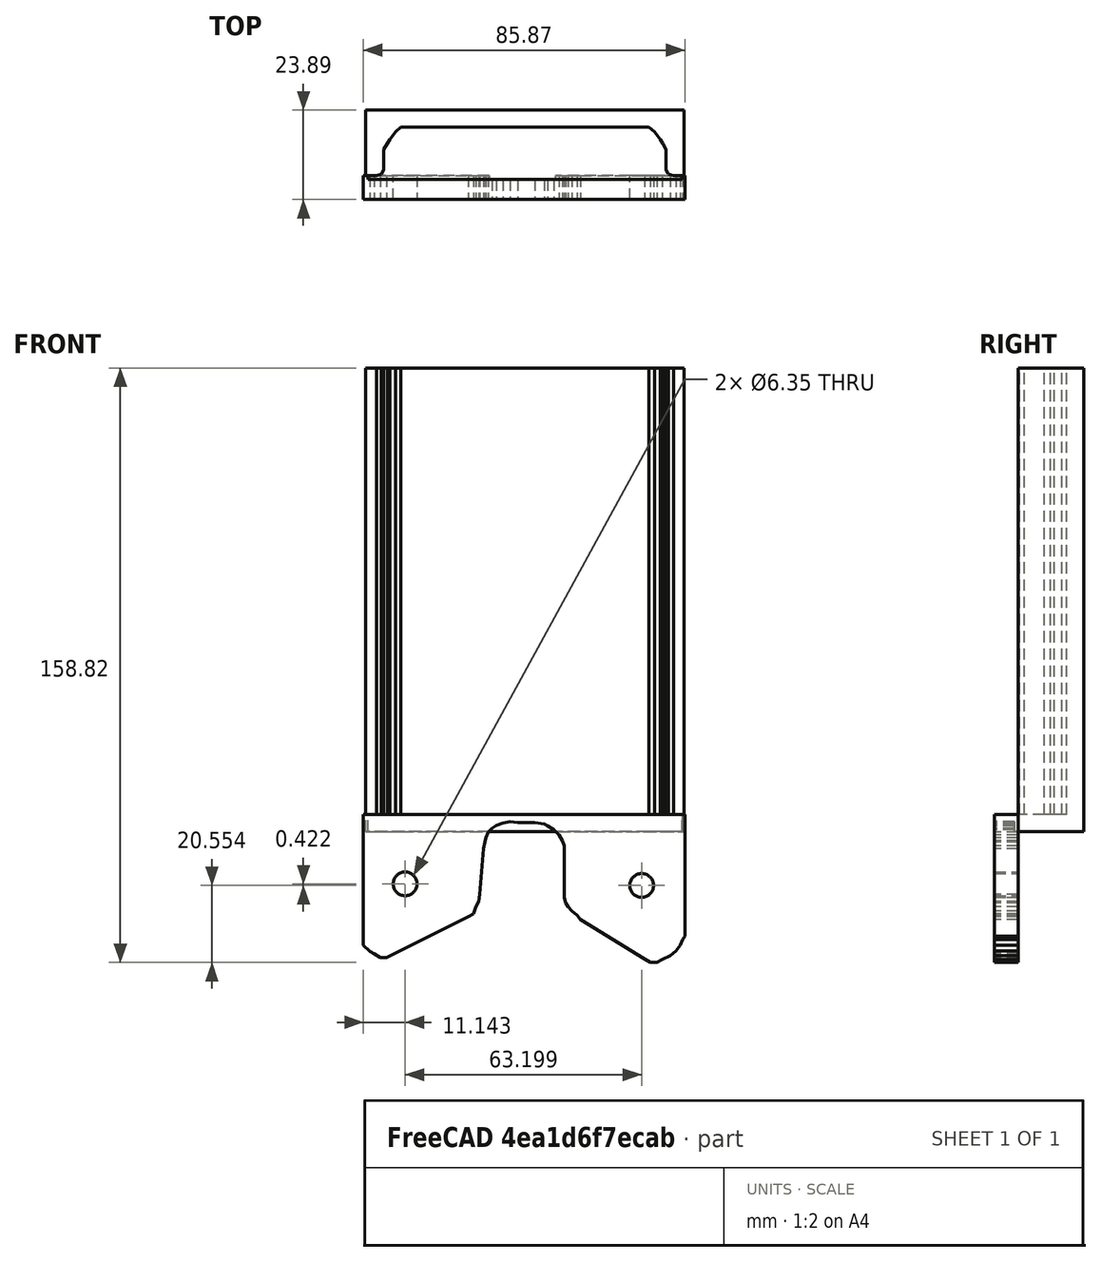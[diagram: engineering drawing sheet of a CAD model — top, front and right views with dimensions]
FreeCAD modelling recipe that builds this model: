
FCSTD DOCUMENT  (FreeCAD 0.20R29177 +426 (Git))
Label: logan-820-cross-slide-cover-model
License: All rights reserved
LicenseURL: http://en.wikipedia.org/wiki/All_rights_reserved
objects: Sketcher::SketchObject×8, Part::Extrusion×3, Mesh::Feature×2, Part::Box×1, Part::FeaturePython×1, Part::Feature×1
note: 14 computed .brp shape members not serialized (recipe doc carries the construction recipe); baked Part::Feature solids carry a one-line shape summary decoded from their .brp

FEATURE [Mesh::Feature] logan_820_cross_slide_cover_logan_cross_slide_bottom_located_new  label="logan-820-cross-slide-cover-logan-cross-slide-bottom-located-new"
FEATURE [Sketcher::SketchObject] Sketch  label="Sketch-through-holes"
  FullyConstrained = false
  MapMode = 3
  Placement = pos=(0,0,0) rot=(1,0,0;1.5708rad)
  Support = -> [logan_820_cross_slide_cover_logan_cross_slide_bottom_located_new]
  sketch-geometry (47):
    g0: Circle CenterX=-32.0171 CenterY=20.9758 CenterZ=0 NormalX=0 NormalY=0 NormalZ=1 AngleXU=0 Radius=3.175
    g1: Circle CenterX=31.1815 CenterY=20.5539 CenterZ=0 NormalX=0 NormalY=0 NormalZ=1 AngleXU=0 Radius=3.175
    g2: LineSegment StartX=-43.158 StartY=39.4781 StartZ=0 EndX=-43.158 EndY=4.59161 EndZ=0
    g3: LineSegment StartX=-43.158 StartY=4.59161 StartZ=0 EndX=-41.4153 EndY=2.95368 EndZ=0
    g4: LineSegment StartX=-41.4153 StartY=2.95368 StartZ=0 EndX=-40.2455 EndY=2.32143 EndZ=0
    g5: LineSegment StartX=-40.2455 StartY=2.32143 StartZ=0 EndX=-38.6261 EndY=1.23818 EndZ=0
    g6: LineSegment StartX=-38.6261 StartY=1.23818 StartZ=0 EndX=-37.0049 EndY=1.32572 EndZ=0
    g7: LineSegment StartX=-37.0049 StartY=1.32572 StartZ=0 EndX=-15.1932 EndY=12.1892 EndZ=0
    g8: LineSegment StartX=-15.1932 StartY=12.1892 StartZ=0 EndX=-13.751 EndY=12.9975 EndZ=0
    g9: LineSegment StartX=-13.751 StartY=12.9975 StartZ=0 EndX=-13.1176 EndY=14.8878 EndZ=0
    g10: LineSegment StartX=-13.1176 StartY=14.8878 StartZ=0 EndX=-12.3949 EndY=16.3276 EndZ=0
    g11: LineSegment StartX=-12.3949 StartY=16.3276 StartZ=0 EndX=-12.1219 EndY=18.1284 EndZ=0
    g12: LineSegment StartX=-12.1219 StartY=18.1284 StartZ=0 EndX=-11.1122 EndY=30.3751 EndZ=0
    g13: LineSegment StartX=-11.1122 StartY=30.3751 StartZ=0 EndX=-10.7491 EndY=32.1758 EndZ=0
    g14: LineSegment StartX=-10.7491 StartY=32.1758 StartZ=0 EndX=-10.3872 EndY=33.256 EndZ=0
    g15: LineSegment StartX=-10.3872 StartY=33.256 StartZ=0 EndX=-9.84445 EndY=34.7862 EndZ=0
    g16: LineSegment StartX=-9.84445 StartY=34.7862 StartZ=0 EndX=-8.76217 EndY=35.7752 EndZ=0
    g17: LineSegment StartX=-8.76217 StartY=35.7752 StartZ=0 EndX=-7.68018 EndY=36.584 EndZ=0
    g18: LineSegment StartX=-7.68018 StartY=36.584 StartZ=0 EndX=-5.87799 EndY=37.2116 EndZ=0
    g19: LineSegment StartX=-5.87799 StartY=37.2116 StartZ=0 EndX=-3.98615 EndY=37.5689 EndZ=0
    g20: LineSegment StartX=-3.98615 StartY=37.5689 StartZ=0 EndX=-1.91503 EndY=37.3856 EndZ=0
    g21: LineSegment StartX=-1.91503 StartY=37.3856 StartZ=0 EndX=0.516609 EndY=37.3856 EndZ=0
    g22: LineSegment StartX=0.516609 StartY=37.3856 StartZ=0 EndX=2.67807 EndY=37.3856 EndZ=0
    g23: LineSegment StartX=2.67807 StartY=37.3856 StartZ=0 EndX=5.10915 EndY=37.0144 EndZ=0
    g24: LineSegment StartX=5.10915 StartY=37.0144 StartZ=0 EndX=6.09898 EndY=36.4725 EndZ=0
    g25: LineSegment StartX=6.09898 StartY=36.4725 StartZ=0 EndX=7.71853 EndY=35.4793 EndZ=0
    g26: LineSegment StartX=7.71853 StartY=35.4793 StartZ=0 EndX=9.15727 EndY=34.0361 EndZ=0
    g27: LineSegment StartX=9.15727 StartY=34.0361 StartZ=0 EndX=9.96543 EndY=32.5038 EndZ=0
    g28: LineSegment StartX=9.96543 StartY=32.5038 StartZ=0 EndX=10.5037 EndY=31.1521 EndZ=0
    g29: LineSegment StartX=10.5037 StartY=31.1521 StartZ=0 EndX=10.5037 EndY=29.621 EndZ=0
    g30: LineSegment StartX=10.5037 StartY=29.621 StartZ=0 EndX=10.5037 EndY=17.283 EndZ=0
    g31: LineSegment StartX=10.5037 StartY=17.283 StartZ=0 EndX=10.8403 EndY=15.9312 EndZ=0
    g32: LineSegment StartX=10.8403 StartY=15.9312 StartZ=0 EndX=11.5591 EndY=14.8494 EndZ=0
    g33: LineSegment StartX=11.5591 StartY=14.8494 StartZ=0 EndX=12.548 EndY=13.7671 EndZ=0
    g34: LineSegment StartX=12.548 StartY=13.7671 StartZ=0 EndX=13.9872 EndY=12.5941 EndZ=0
    g35: LineSegment StartX=13.9872 StartY=12.5941 StartZ=0 EndX=14.7961 EndY=11.5121 EndZ=0
    g36: LineSegment StartX=14.7961 StartY=11.5121 StartZ=0 EndX=31.9812 EndY=0.85818 EndZ=0
    g37: LineSegment StartX=31.9812 StartY=0.85818 StartZ=0 EndX=33.5109 EndY=0 EndZ=0
    g38: LineSegment StartX=33.5109 StartY=0 StartZ=0 EndX=35.3127 EndY=0 EndZ=0
    g39: LineSegment StartX=35.3127 StartY=0 StartZ=0 EndX=36.6642 EndY=0.760835 EndZ=0
    g40: LineSegment StartX=36.6642 StartY=0.760835 StartZ=0 EndX=38.8273 EndY=1.8382 EndZ=0
    g41: LineSegment StartX=38.8273 StartY=1.8382 StartZ=0 EndX=40.3602 EndY=3.00661 EndZ=0
    g42: LineSegment StartX=40.3602 StartY=3.00661 StartZ=0 EndX=41.4433 EndY=4.53596 EndZ=0
    g43: LineSegment StartX=41.4433 StartY=4.53596 StartZ=0 EndX=42.0762 EndY=6.15608 EndZ=0
    g44: LineSegment StartX=42.0762 StartY=6.15608 StartZ=0 EndX=42.7079 EndY=6.96564 EndZ=0
    g45: LineSegment StartX=42.7079 StartY=6.96564 StartZ=0 EndX=42.7079 EndY=39.4781 EndZ=0
    g46: LineSegment StartX=42.7079 StartY=39.4781 StartZ=0 EndX=-43.158 EndY=39.4781 EndZ=0
  constraints (57):
    c: Distance(g1,g0) = 63.2
    c: Diameter(g0) = 6.35
    c: Diameter(g1) = 6.35
    c: Vertical(g2)
    c: Coincident(g2,g3)
    c: Coincident(g3,g4)
    c: Coincident(g4,g5)
    c: Coincident(g5,g6)
    c: Coincident(g6,g7)
    c: Coincident(g7,g8)
    c: Coincident(g8,g9)
    c: Coincident(g9,g10)
    c: Coincident(g10,g11)
    c: Coincident(g11,g12)
    c: Coincident(g12,g13)
    c: Coincident(g13,g14)
    c: Coincident(g14,g15)
    c: Coincident(g15,g16)
    c: Coincident(g16,g17)
    c: Coincident(g17,g18)
    c: Coincident(g18,g19)
    c: Coincident(g19,g20)
    c: Coincident(g20,g21)
    c: Horizontal(g21)
    c: Coincident(g21,g22)
    c: Horizontal(g22)
    c: Coincident(g22,g23)
    c: Coincident(g23,g24)
    c: Coincident(g24,g25)
    c: Coincident(g25,g26)
    c: Coincident(g26,g27)
    c: Coincident(g27,g28)
    c: Coincident(g28,g29)
    c: Vertical(g29)
    c: Coincident(g29,g30)
    c: Vertical(g30)
    c: Coincident(g30,g31)
    c: Coincident(g31,g32)
    c: Coincident(g32,g33)
    c: Coincident(g33,g34)
    c: Coincident(g34,g35)
    c: Coincident(g35,g36)
    c: Coincident(g36,g37)
    c: PointOnObject(g37,g-1)
    c: Coincident(g37,g38)
    c: PointOnObject(g38,g-1)
    c: Coincident(g38,g39)
    c: Coincident(g39,g40)
    c: Coincident(g40,g41)
    c: Coincident(g41,g42)
    c: Coincident(g42,g43)
    c: Coincident(g43,g44)
    c: Coincident(g44,g45)
    c: Vertical(g45)
    c: Coincident(g45,g46)
    c: Coincident(g46,g2)
    c: Horizontal(g46)
FEATURE [Sketcher::SketchObject] Sketch001  label="sketch-side"
  FullyConstrained = false
  MapMode = 4
  Placement = pos=(0,0,0) rot=(0.707107,0,0.707107;3.14159rad)
  Support = -> [Sketch]
  sketch-geometry (23):
    g0: LineSegment StartX=41.088 StartY=-4.31506 StartZ=0 EndX=39.2016 EndY=-13.0361 EndZ=0
    g1: LineSegment StartX=39.2016 StartY=-13.0361 StartZ=0 EndX=38.7187 EndY=-13.8209 EndZ=0
    g2: LineSegment StartX=38.7187 StartY=-13.8209 StartZ=0 EndX=37.9943 EndY=-14.7264 EndZ=0
    g3: LineSegment StartX=37.9943 StartY=-14.7264 StartZ=0 EndX=37.0283 EndY=-14.9075 EndZ=0
    g4: LineSegment StartX=37.0283 StartY=-14.9075 StartZ=0 EndX=36.0624 EndY=-15.149 EndZ=0
    g5: LineSegment StartX=36.0624 StartY=-15.149 StartZ=0 EndX=4.10285 EndY=-13.8406 EndZ=0
    g6: LineSegment StartX=4.10285 StartY=-13.8406 StartZ=0 EndX=3.29351 EndY=-13.962 EndZ=0
    g7: LineSegment StartX=3.29351 StartY=-13.962 StartZ=0 EndX=2.40323 EndY=-14.1238 EndZ=0
    g8: LineSegment StartX=2.40323 StartY=-14.1238 StartZ=0 EndX=1.59389 EndY=-14.6095 EndZ=0
    g9: LineSegment StartX=1.59389 StartY=-14.6095 StartZ=0 EndX=1.14876 EndY=-14.9332 EndZ=0
    g10: LineSegment StartX=1.14876 StartY=-14.9332 StartZ=0 EndX=0.905955 EndY=-15.4188 EndZ=0
    g11: LineSegment StartX=0.905955 StartY=-15.4188 StartZ=0 EndX=0.744088 EndY=-16.2281 EndZ=0
    g12: LineSegment StartX=0.744088 StartY=-16.2281 StartZ=0 EndX=0.460819 EndY=-19.2632 EndZ=0
    g13: LineSegment StartX=0.460819 StartY=-19.2632 StartZ=0 EndX=42.3738 EndY=-19.2632 EndZ=0
    g14: LineSegment StartX=42.3738 StartY=-19.2632 StartZ=0 EndX=42.9637 EndY=-18.7401 EndZ=0
    g15: LineSegment StartX=42.9637 StartY=-18.7401 StartZ=0 EndX=43.9223 EndY=-17.8553 EndZ=0
    g16: LineSegment StartX=43.9223 StartY=-17.8553 StartZ=0 EndX=44.291 EndY=-16.6755 EndZ=0
    g17: LineSegment StartX=44.291 StartY=-16.6755 StartZ=0 EndX=163.958 EndY=-16.6755 EndZ=0
    g18: LineSegment StartX=163.958 StartY=-16.6755 StartZ=0 EndX=162.557 EndY=-5.78977 EndZ=0
    g19: LineSegment StartX=162.557 StartY=-5.78977 StartZ=0 EndX=161.967 EndY=-5.12615 EndZ=0
    g20: LineSegment StartX=161.967 StartY=-5.12615 StartZ=0 EndX=161.156 EndY=-4.83121 EndZ=0
    g21: LineSegment StartX=161.156 StartY=-4.83121 StartZ=0 EndX=159.755 EndY=-4.31506 EndZ=0
    g22: LineSegment StartX=159.755 StartY=-4.31506 StartZ=0 EndX=41.088 EndY=-4.31506 EndZ=0
  constraints (26):
    c: Coincident(g0,g1)
    c: Coincident(g1,g2)
    c: Coincident(g2,g3)
    c: Coincident(g3,g4)
    c: Coincident(g4,g5)
    c: Coincident(g5,g6)
    c: Coincident(g6,g7)
    c: Coincident(g7,g8)
    c: Coincident(g8,g9)
    c: Coincident(g9,g10)
    c: Coincident(g10,g11)
    c: Coincident(g11,g12)
    c: Coincident(g12,g13)
    c: Horizontal(g13)
    c: Coincident(g13,g14)
    c: Coincident(g14,g15)
    c: Coincident(g15,g16)
    c: Coincident(g16,g17)
    c: Horizontal(g17)
    c: Coincident(g17,g18)
    c: Coincident(g18,g19)
    c: Coincident(g19,g20)
    c: Coincident(g20,g21)
    c: Coincident(g21,g22)
    c: Coincident(g22,g0)
    c: Horizontal(g22)
FEATURE [Sketcher::SketchObject] Sketch002  label="sketch-side-of-mount"
  FullyConstrained = false
  MapMode = 4
  Placement = pos=(0,0,0) rot=(0.707107,0,0.707107;3.14159rad)
  Support = -> [Sketch]
  sketch-geometry (23):
    g0: LineSegment StartX=45.8302 StartY=-2.4673 StartZ=0 EndX=43.8508 EndY=-1.76256 EndZ=0
    g1: LineSegment StartX=43.8508 StartY=-1.76256 StartZ=0 EndX=42.5311 EndY=-1.76256 EndZ=0
    g2: LineSegment StartX=42.5311 StartY=-1.76256 StartZ=0 EndX=41.3419 EndY=-2.70137 EndZ=0
    g3: LineSegment StartX=41.3419 StartY=-2.70137 StartZ=0 EndX=40.7205 EndY=-4.36669 EndZ=0
    g4: LineSegment StartX=40.7205 StartY=-4.36669 StartZ=0 EndX=39.1914 EndY=-14.3075 EndZ=0
    g5: LineSegment StartX=39.1914 StartY=-14.3075 StartZ=0 EndX=38.5546 EndY=-15.3128 EndZ=0
    g6: LineSegment StartX=38.5546 StartY=-15.3128 StartZ=0 EndX=37.46 EndY=-15.5584 EndZ=0
    g7: LineSegment StartX=37.46 StartY=-15.5584 StartZ=0 EndX=36.4703 EndY=-15.5584 EndZ=0
    g8: LineSegment StartX=36.4703 StartY=-15.5584 StartZ=0 EndX=3.92285 EndY=-15.5584 EndZ=0
    g9: LineSegment StartX=3.92285 StartY=-15.5584 StartZ=0 EndX=2.8393 EndY=-14.8509 EndZ=0
    g10: LineSegment StartX=2.8393 StartY=-14.8509 StartZ=0 EndX=1.93962 EndY=-15.1134 EndZ=0
    g11: LineSegment StartX=1.93962 StartY=-15.1134 StartZ=0 EndX=1.34593 EndY=-15.55 EndZ=0
    g12: LineSegment StartX=1.34593 StartY=-15.55 StartZ=0 EndX=0.879963 EndY=-16.2857 EndZ=0
    g13: LineSegment StartX=0.879963 StartY=-16.2857 StartZ=0 EndX=0.654005 EndY=-16.9553 EndZ=0
    g14: LineSegment StartX=0.654005 StartY=-16.9553 StartZ=0 EndX=0.654005 EndY=-18.5249 EndZ=0
    g15: LineSegment StartX=0.654005 StartY=-18.5249 StartZ=0 EndX=0.346687 EndY=-19.3181 EndZ=0
    g16: LineSegment StartX=0.346687 StartY=-19.3181 StartZ=0 EndX=0.178274 EndY=-19.8656 EndZ=0
    g17: LineSegment StartX=0.178274 StartY=-19.8656 StartZ=0 EndX=38.3328 EndY=-19.8656 EndZ=0
    g18: LineSegment StartX=38.3328 StartY=-19.8656 StartZ=0 EndX=42.7484 EndY=-19.8656 EndZ=0
    g19: LineSegment StartX=42.7484 StartY=-19.8656 StartZ=0 EndX=45.3112 EndY=-15.7356 EndZ=0
    g20: LineSegment StartX=45.3112 StartY=-15.7356 StartZ=0 EndX=70.0028 EndY=-15.7356 EndZ=0
    g21: LineSegment StartX=70.0028 StartY=-15.7356 StartZ=0 EndX=70.0028 EndY=-2.4673 EndZ=0
    g22: LineSegment StartX=70.0028 StartY=-2.4673 StartZ=0 EndX=45.8302 EndY=-2.4673 EndZ=0
  constraints (32):
    c: Coincident(g0,g1)
    c: Horizontal(g1)
    c: Coincident(g1,g2)
    c: Coincident(g2,g3)
    c: Coincident(g3,g4)
    c: Coincident(g4,g5)
    c: Coincident(g5,g6)
    c: Coincident(g6,g7)
    c: Horizontal(g7)
    c: Coincident(g7,g8)
    c: Horizontal(g8)
    c: Coincident(g8,g9)
    c: Coincident(g9,g10)
    c: Coincident(g10,g11)
    c: Coincident(g11,g12)
    c: Coincident(g12,g13)
    c: Coincident(g13,g14)
    c: Vertical(g14)
    c: Coincident(g14,g15)
    c: Coincident(g15,g16)
    c: Coincident(g16,g17)
    c: Horizontal(g17)
    c: Coincident(g17,g18)
    c: Horizontal(g18)
    c: Coincident(g18,g19)
    c: Coincident(g19,g20)
    c: Horizontal(g20)
    c: Coincident(g20,g21)
    c: Vertical(g21)
    c: Coincident(g21,g22)
    c: Coincident(g22,g0)
    c: Horizontal(g22)
FEATURE [Sketcher::SketchObject] Sketch003  label="sketch-end"
  FullyConstrained = false
  sketch-geometry (26):
    g0: LineSegment StartX=-43.5422 StartY=19.1592 StartZ=0 EndX=-43.5422 EndY=0.579213 EndZ=0
    g1: LineSegment StartX=-43.5422 StartY=0.579213 StartZ=0 EndX=-40.4943 EndY=0.579213 EndZ=0
    g2: LineSegment StartX=-40.4943 StartY=0.579213 StartZ=0 EndX=-39.3512 EndY=0.877175 EndZ=0
    g3: LineSegment StartX=-39.3512 StartY=0.877175 StartZ=0 EndX=-38.5964 EndY=3.02767 EndZ=0
    g4: LineSegment StartX=-38.5964 StartY=3.02767 StartZ=0 EndX=-38.5421 EndY=6.3087 EndZ=0
    g5: LineSegment StartX=-38.5421 StartY=6.3087 StartZ=0 EndX=-38.3105 EndY=8.54246 EndZ=0
    g6: LineSegment StartX=-38.3105 StartY=8.54246 StartZ=0 EndX=-37.4257 EndY=10.5333 EndZ=0
    g7: LineSegment StartX=-37.4257 StartY=10.5333 StartZ=0 EndX=-35.656 EndY=12.2292 EndZ=0
    g8: LineSegment StartX=-35.656 StartY=12.2292 StartZ=0 EndX=-34.1813 EndY=13.409 EndZ=0
    g9: LineSegment StartX=-34.1813 StartY=13.409 StartZ=0 EndX=-32.7803 EndY=13.704 EndZ=0
    g10: LineSegment StartX=-32.7803 StartY=13.704 StartZ=0 EndX=30.8535 EndY=13.704 EndZ=0
    g11: LineSegment StartX=30.8535 StartY=13.704 StartZ=0 EndX=33.213 EndY=13.0403 EndZ=0
    g12: LineSegment StartX=33.213 StartY=13.0403 StartZ=0 EndX=34.3191 EndY=12.2292 EndZ=0
    g13: LineSegment StartX=34.3191 StartY=12.2292 StartZ=0 EndX=35.8675 EndY=10.6808 EndZ=0
    g14: LineSegment StartX=35.8675 StartY=10.6808 StartZ=0 EndX=37.0473 EndY=8.8374 EndZ=0
    g15: LineSegment StartX=37.0473 StartY=8.8374 StartZ=0 EndX=37.1948 EndY=7.65763 EndZ=0
    g16: LineSegment StartX=37.1948 StartY=7.65763 StartZ=0 EndX=37.4897 EndY=6.5516 EndZ=0
    g17: LineSegment StartX=37.4897 StartY=6.5516 StartZ=0 EndX=38.0796 EndY=2.86482 EndZ=0
    g18: LineSegment StartX=38.0796 StartY=2.86482 StartZ=0 EndX=38.5957 EndY=1.68505 EndZ=0
    g19: LineSegment StartX=38.5957 StartY=1.68505 StartZ=0 EndX=39.2594 EndY=1.09516 EndZ=0
    g20: LineSegment StartX=39.2594 StartY=1.09516 StartZ=0 EndX=39.923 EndY=0.583043 EndZ=0
    g21: LineSegment StartX=39.923 StartY=0.583043 StartZ=0 EndX=42.2078 EndY=0.583043 EndZ=0
    g22: LineSegment StartX=42.2078 StartY=0.583043 StartZ=0 EndX=42.2078 EndY=19.163 EndZ=0
    g23: LineSegment StartX=42.2078 StartY=19.163 StartZ=0 EndX=-43.5422 EndY=19.163 EndZ=0
    g24: GeomPoint X=-39.0502 Y=1.73483 Z=0
    g25: GeomPoint X=-40.412 Y=0.600657 Z=0
  constraints (34):
    c: Vertical(g0)
    c: Coincident(g0,g1)
    c: Coincident(g1,g2)
    c: Coincident(g2,g3)
    c: Coincident(g3,g4)
    c: Coincident(g4,g5)
    c: Coincident(g5,g6)
    c: Coincident(g6,g7)
    c: Coincident(g7,g8)
    c: Coincident(g8,g9)
    c: Coincident(g9,g10)
    c: Horizontal(g10)
    c: Coincident(g10,g11)
    c: Coincident(g11,g12)
    c: Coincident(g12,g13)
    c: Coincident(g13,g14)
    c: Coincident(g14,g15)
    c: Coincident(g15,g16)
    c: Coincident(g16,g17)
    c: Coincident(g17,g18)
    c: Coincident(g18,g19)
    c: Coincident(g19,g20)
    c: Coincident(g20,g21)
    c: Coincident(g21,g22)
    c: Vertical(g22)
    c: Coincident(g22,g23)
    c: Horizontal(g23)
    c: Horizontal(g21)
    c: Distance(g23) = 85.75
    c: Distance(g22) = 18.58
    c: Equal(g0,g22)
    c: PointOnObject(g24,g3)
    c: PointOnObject(g25,g2)
    c: Horizontal(g1)
FEATURE [Part::Extrusion] Extrude  label="Extrude-main-cover-first-attempt"
  Base = -> Sketch003
  Dir = (0,0,1)
  DirMode = 2
  FaceMakerClass = Part::FaceMakerBullseye
  LengthFwd = 120.65
  LengthRev = 0
  Placement = pos=(0,0,38.1) rot=(0,0,1;0rad)
  Solid = false
  Symmetric = false
FEATURE [Part::Extrusion] Extrude001  label="extrude-mount"
  Base = -> Sketch
  Dir = (0,-1,2e-16)
  DirMode = 2
  FaceMakerClass = Part::FaceMakerBullseye
  LengthFwd = 6.35
  LengthRev = 0
  Solid = true
  Symmetric = false
FEATURE [Sketcher::SketchObject] Sketch004  label="sketch-end-half"
  FullyConstrained = false
  sketch-geometry (20):
    g0: LineSegment StartX=-0.0341461 StartY=13.7403 StartZ=0 EndX=30.8542 EndY=13.7403 EndZ=0
    g1: LineSegment StartX=30.8542 StartY=13.7403 StartZ=0 EndX=33.213 EndY=13.0403 EndZ=0
    g2: LineSegment StartX=33.213 StartY=13.0403 StartZ=0 EndX=34.3191 EndY=12.2292 EndZ=0
    g3: LineSegment StartX=34.3191 StartY=12.2292 StartZ=0 EndX=35.8675 EndY=10.6808 EndZ=0
    g4: LineSegment StartX=35.8675 StartY=10.6808 StartZ=0 EndX=37.0473 EndY=8.8374 EndZ=0
    g5: LineSegment StartX=37.0473 StartY=8.8374 StartZ=0 EndX=37.251 EndY=7.64431 EndZ=0
    g6: LineSegment StartX=37.251 StartY=7.64431 StartZ=0 EndX=37.4897 EndY=6.5516 EndZ=0
    g7: LineSegment StartX=37.4897 StartY=6.5516 StartZ=0 EndX=38.0796 EndY=2.86482 EndZ=0
    g8: LineSegment StartX=38.0796 StartY=2.86482 StartZ=0 EndX=38.5957 EndY=1.68505 EndZ=0
    g9: LineSegment StartX=38.5957 StartY=1.68505 StartZ=0 EndX=39.2594 EndY=1.09516 EndZ=0
    g10: LineSegment StartX=39.2594 StartY=1.09516 StartZ=0 EndX=39.93 EndY=0.6 EndZ=0
    g11: LineSegment StartX=39.93 StartY=0.6 StartZ=0 EndX=42.21 EndY=0.6 EndZ=0
    g12: LineSegment StartX=42.21 StartY=0.6 StartZ=0 EndX=42.21 EndY=19.18 EndZ=0
    g13: LineSegment StartX=42.21 StartY=19.18 StartZ=0 EndX=-43.54 EndY=19.18 EndZ=0
    g14: GeomPoint X=-0.0903729 Y=19.18 Z=0
    g15: GeomPoint X=-0.025795 Y=13.7403 Z=0
    g16: GeomPoint X=42.21 Y=0 Z=0
    g17: GeomPoint X=39.93 Y=0 Z=0
    g18: GeomPoint X=0 Y=0.6 Z=0
    g19: GeomPoint X=42.21 Y=13.3891 Z=0
  constraints (32):
    c: Horizontal(g0)
    c: Coincident(g0,g1)
    c: Coincident(g1,g2)
    c: Coincident(g2,g3)
    c: Coincident(g3,g4)
    c: Coincident(g4,g5)
    c: Coincident(g5,g6)
    c: Coincident(g6,g7)
    c: Coincident(g7,g8)
    c: Coincident(g8,g9)
    c: Coincident(g9,g10)
    c: Coincident(g10,g11)
    c: Coincident(g11,g12)
    c: Vertical(g12)
    c: Coincident(g12,g13)
    c: Horizontal(g13)
    c: Horizontal(g11)
    c: Distance(g13) = 85.75
    c: Distance(g12) = 18.58
    c: PointOnObject(g14,g13)
    c: PointOnObject(g15,g0)
    c: PointOnObject(g16,g-1)
    c: PointOnObject(g17,g-1)
    c: Distance(g16,g11) = 0.6
    c: Distance(g10,g17) = 0.6
    c: PointOnObject(g18,g-2)
    c: Distance(g-1,g18) = 0.6
    c: Distance(g18,g11) = 42.21
    c: Distance(g10,g11) = 2.28
    c: Distance(g0,g15) = 30.88
    c: PointOnObject(g19,g12)
    c: Distance(g14,g0) = 5.44
FEATURE [Sketcher::SketchObject] Sketch005
  FullyConstrained = false
  sketch-geometry (13):
    g0: LineSegment StartX=0 StartY=18.5413 StartZ=0 EndX=42.57 EndY=18.5413 EndZ=0
    g1: LineSegment StartX=42.57 StartY=18.5413 StartZ=0 EndX=42.57 EndY=1.01296 EndZ=0
    g2: LineSegment StartX=42.57 StartY=1.01296 StartZ=0 EndX=39.6826 EndY=1.01296 EndZ=0
    g3: LineSegment StartX=39.6826 StartY=1.01296 StartZ=0 EndX=38.3774 EndY=1.3859 EndZ=0
    g4: LineSegment StartX=38.3774 StartY=1.3859 StartZ=0 EndX=37.7247 EndY=2.59796 EndZ=0
    g5: LineSegment StartX=37.7247 StartY=2.59796 StartZ=0 EndX=37.7247 EndY=8.00564 EndZ=0
    g6: LineSegment StartX=37.7247 StartY=8.00564 StartZ=0 EndX=36.7923 EndY=9.68388 EndZ=0
    g7: LineSegment StartX=36.7923 StartY=9.68388 StartZ=0 EndX=36.1211 EndY=10.6977 EndZ=0
    g8: LineSegment StartX=36.1211 StartY=10.6977 StartZ=0 EndX=34.642 EndY=12.6601 EndZ=0
    g9: LineSegment StartX=34.642 StartY=12.6601 StartZ=0 EndX=33.1688 EndY=13.9727 EndZ=0
    g10: LineSegment StartX=33.1688 StartY=13.9727 StartZ=0 EndX=0 EndY=13.9727 EndZ=0
    g11: LineSegment StartX=0 StartY=13.9727 StartZ=0 EndX=0 EndY=18.5413 EndZ=0
    g12: GeomPoint X=42.57 Y=14.0374 Z=0
  constraints (21):
    c: PointOnObject(g0,g-2)
    c: Horizontal(g0)
    c: Coincident(g0,g1)
    c: Vertical(g1)
    c: Coincident(g1,g2)
    c: Horizontal(g2)
    c: Coincident(g2,g3)
    c: Coincident(g3,g4)
    c: Coincident(g4,g5)
    c: Coincident(g5,g6)
    c: Coincident(g6,g7)
    c: Coincident(g7,g8)
    c: Coincident(g8,g9)
    c: Coincident(g9,g10)
    c: PointOnObject(g10,g-2)
    c: Coincident(g10,g11)
    c: PointOnObject(g11,g-2)
    c: Horizontal(g10)
    c: Vertical(g5)
    c: Distance(g0) = 42.57
    c: PointOnObject(g12,g1)
FEATURE [Sketcher::SketchObject] MirroredSketch
  FullyConstrained = false
  Placement = pos=(-1,0,0) rot=(0,0,1;0rad)
  sketch-geometry (13):
    g0: LineSegment StartX=0 StartY=18.5413 StartZ=0 EndX=-42.57 EndY=18.5413 EndZ=0
    g1: LineSegment StartX=-42.57 StartY=18.5413 StartZ=0 EndX=-42.57 EndY=1.01296 EndZ=0
    g2: LineSegment StartX=-42.57 StartY=1.01296 StartZ=0 EndX=-39.6826 EndY=1.01296 EndZ=0
    g3: LineSegment StartX=-39.6826 StartY=1.01296 StartZ=0 EndX=-38.3774 EndY=1.3859 EndZ=0
    g4: LineSegment StartX=-38.3774 StartY=1.3859 StartZ=0 EndX=-37.7247 EndY=2.59796 EndZ=0
    g5: LineSegment StartX=-37.7247 StartY=2.59796 StartZ=0 EndX=-37.7247 EndY=8.00564 EndZ=0
    g6: LineSegment StartX=-37.7247 StartY=8.00564 StartZ=0 EndX=-36.7923 EndY=9.68388 EndZ=0
    g7: LineSegment StartX=-36.7923 StartY=9.68388 StartZ=0 EndX=-36.1211 EndY=10.6977 EndZ=0
    g8: LineSegment StartX=-36.1211 StartY=10.6977 StartZ=0 EndX=-34.642 EndY=12.6601 EndZ=0
    g9: LineSegment StartX=-34.642 StartY=12.6601 StartZ=0 EndX=-33.1688 EndY=13.9727 EndZ=0
    g10: LineSegment StartX=-33.1688 StartY=13.9727 StartZ=0 EndX=0 EndY=13.9727 EndZ=0
    g11: LineSegment StartX=0 StartY=13.9727 StartZ=0 EndX=0 EndY=18.5413 EndZ=0
    g12: GeomPoint X=-42.57 Y=14.0374 Z=0
  constraints (18):
    c: Horizontal(g0)
    c: Coincident(g0,g1)
    c: Vertical(g1)
    c: Coincident(g1,g2)
    c: Horizontal(g2)
    c: Coincident(g2,g3)
    c: Coincident(g3,g4)
    c: Coincident(g4,g5)
    c: Coincident(g5,g6)
    c: Coincident(g6,g7)
    c: Coincident(g7,g8)
    c: Coincident(g8,g9)
    c: Coincident(g9,g10)
    c: Coincident(g10,g11)
    c: Horizontal(g10)
    c: Vertical(g5)
    c: Distance(g0) = 42.57
    c: PointOnObject(g12,g1)
FEATURE [Sketcher::SketchObject] Sketch006  label="sketch-main-cover"
  FullyConstrained = false
  sketch-geometry (24):
    g0: LineSegment StartX=0 StartY=18.5413 StartZ=0 EndX=42.57 EndY=18.5413 EndZ=0
    g1: LineSegment StartX=42.57 StartY=18.5413 StartZ=0 EndX=42.57 EndY=1.01296 EndZ=0
    g2: LineSegment StartX=42.57 StartY=1.01296 StartZ=0 EndX=39.6826 EndY=1.01296 EndZ=0
    g3: LineSegment StartX=39.6826 StartY=1.01296 StartZ=0 EndX=38.3774 EndY=1.3859 EndZ=0
    g4: LineSegment StartX=38.3774 StartY=1.3859 StartZ=0 EndX=37.7247 EndY=2.59796 EndZ=0
    g5: LineSegment StartX=37.7247 StartY=2.59796 StartZ=0 EndX=37.7247 EndY=8.00564 EndZ=0
    g6: LineSegment StartX=37.7247 StartY=8.00564 StartZ=0 EndX=36.7923 EndY=9.68388 EndZ=0
    g7: LineSegment StartX=36.7923 StartY=9.68388 StartZ=0 EndX=36.1211 EndY=10.6977 EndZ=0
    g8: LineSegment StartX=36.1211 StartY=10.6977 StartZ=0 EndX=34.642 EndY=12.6601 EndZ=0
    g9: LineSegment StartX=34.642 StartY=12.6601 StartZ=0 EndX=33.1688 EndY=13.9727 EndZ=0
    g10: LineSegment StartX=33.1688 StartY=13.9727 StartZ=0 EndX=0 EndY=13.9727 EndZ=0
    g11: GeomPoint X=42.57 Y=14.0374 Z=0
    g12: LineSegment StartX=0 StartY=18.5413 StartZ=0 EndX=-42.57 EndY=18.5413 EndZ=0
    g13: LineSegment StartX=-42.57 StartY=18.5413 StartZ=0 EndX=-42.57 EndY=1.01296 EndZ=0
    g14: LineSegment StartX=-42.57 StartY=1.01296 StartZ=0 EndX=-39.6826 EndY=1.01296 EndZ=0
    g15: LineSegment StartX=-39.6826 StartY=1.01296 StartZ=0 EndX=-38.3774 EndY=1.3859 EndZ=0
    g16: LineSegment StartX=-38.3774 StartY=1.3859 StartZ=0 EndX=-37.7247 EndY=2.59796 EndZ=0
    g17: LineSegment StartX=-37.7247 StartY=2.59796 StartZ=0 EndX=-37.7247 EndY=8.00564 EndZ=0
    g18: LineSegment StartX=-37.7247 StartY=8.00564 StartZ=0 EndX=-36.7923 EndY=9.68388 EndZ=0
    g19: LineSegment StartX=-36.7923 StartY=9.68388 StartZ=0 EndX=-36.1211 EndY=10.6977 EndZ=0
    g20: LineSegment StartX=-36.1211 StartY=10.6977 StartZ=0 EndX=-34.642 EndY=12.6601 EndZ=0
    g21: LineSegment StartX=-34.642 StartY=12.6601 StartZ=0 EndX=-33.1688 EndY=13.9727 EndZ=0
    g22: LineSegment StartX=-33.1688 StartY=13.9727 StartZ=0 EndX=0 EndY=13.9727 EndZ=0
    g23: GeomPoint X=-42.57 Y=14.0374 Z=0
  constraints (36):
    c: PointOnObject(g0,g-2)
    c: Horizontal(g0)
    c: Coincident(g0,g1)
    c: Vertical(g1)
    c: Coincident(g1,g2)
    c: Horizontal(g2)
    c: Coincident(g2,g3)
    c: Coincident(g3,g4)
    c: Coincident(g4,g5)
    c: Coincident(g5,g6)
    c: Coincident(g6,g7)
    c: Coincident(g7,g8)
    c: Coincident(g8,g9)
    c: Coincident(g9,g10)
    c: PointOnObject(g10,g-2)
    c: Horizontal(g10)
    c: Vertical(g5)
    c: Distance(g0) = 42.57
    c: PointOnObject(g11,g1)
    c: Horizontal(g12)
    c: Coincident(g12,g13)
    c: Vertical(g13)
    c: Coincident(g13,g14)
    c: Horizontal(g14)
    c: Coincident(g14,g15)
    c: Coincident(g15,g16)
    c: Coincident(g16,g17)
    c: Coincident(g17,g18)
    c: Coincident(g18,g19)
    c: Coincident(g19,g20)
    c: Coincident(g20,g21)
    c: Coincident(g21,g22)
    c: Horizontal(g22)
    c: Vertical(g17)
    c: Distance(g12) = 42.57
    c: PointOnObject(g23,g13)
FEATURE [Part::Extrusion] Extrude002  label="extrude-main-cover"
  Base = -> Sketch006
  Dir = (0,0,1)
  DirMode = 2
  FaceMakerClass = Part::FaceMakerBullseye
  LengthFwd = 123.825
  LengthRev = 0
  Placement = pos=(0,-1,35) rot=(0,0,1;0rad)
  Solid = true
  Symmetric = false
FEATURE [Part::Box] Box  label="cover-mount-join"
  AttacherType = Attacher::AttachEngine3D
  Height = 4.5
  Length = 84
  Placement = pos=(-42,-1,35) rot=(0,0,1;0rad)
  Width = 18
FEATURE [Part::FeaturePython] Connect  label="Connected-cover-mount"  # WARN: FeaturePython — macro-defined, semantics opaque (R4)
  Objects = -> [Box,Extrude002,Extrude001]
  Tolerance = 0
FEATURE [Part::Feature] Connect_solid  label="Connected-cover-mount (Solid)"
  shape: bbox 85.87 x 23.89 x 158.8 mm, 81 faces (baked)
FEATURE [Mesh::Feature] Mesh  label="Connected-cover-mount (Solid) (Meshed)"
